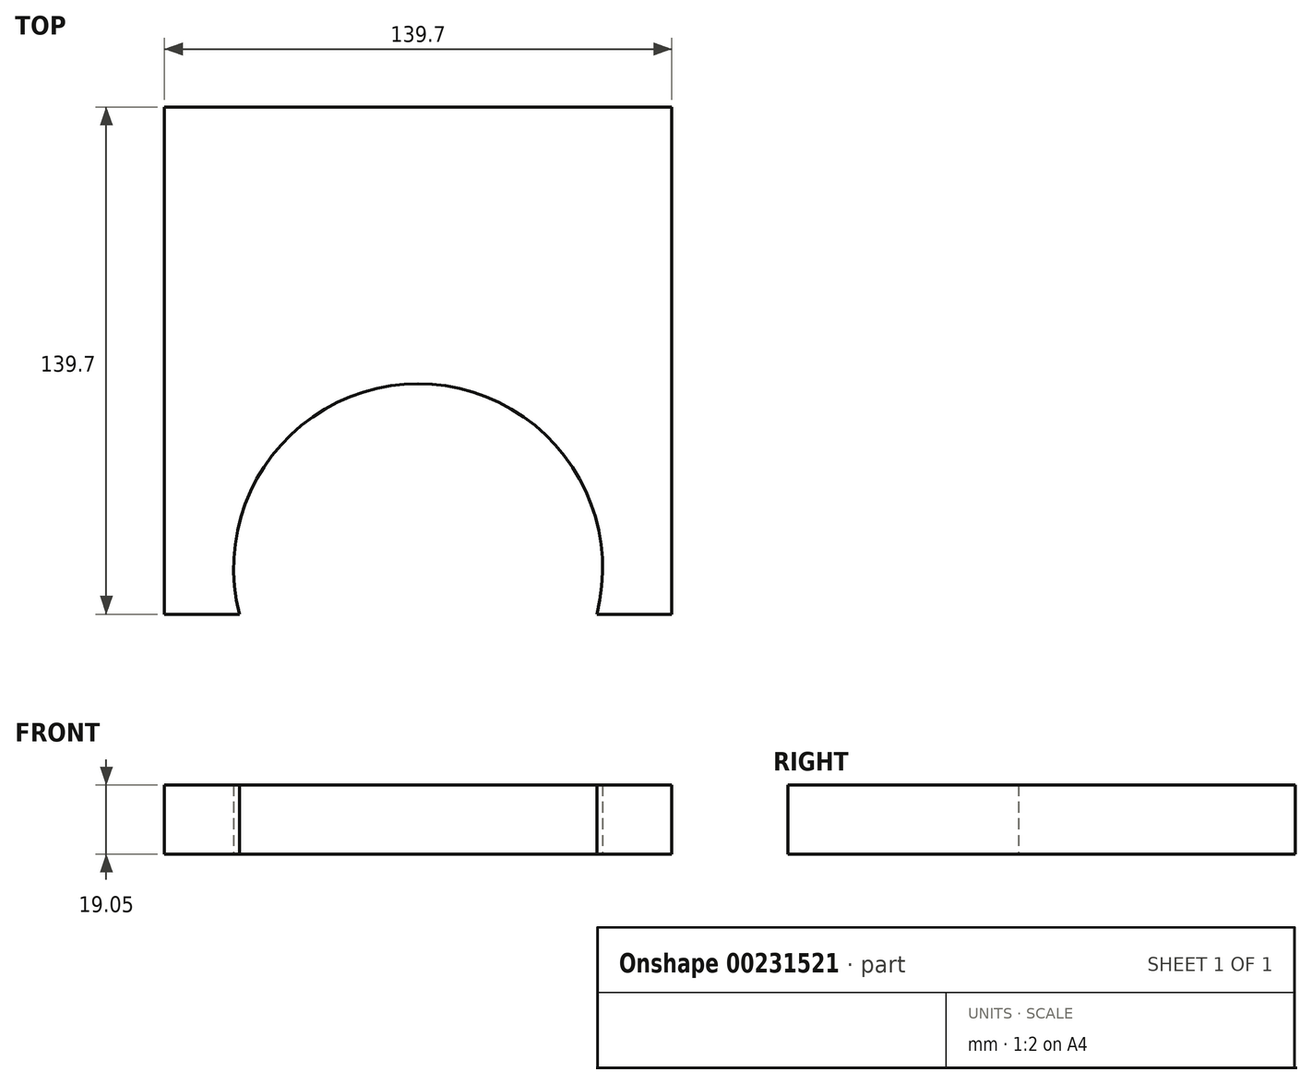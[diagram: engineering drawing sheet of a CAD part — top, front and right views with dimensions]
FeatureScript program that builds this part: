
annotation { "Feature Type Name" : "Feature", "Feature Type Description" : "" }
export const myFeature = defineFeature(function(context is Context, id is Id, definition is map)
    precondition{}
    {
        {
            var Q0;
            Q0=qCreatedBy(makeId("Top.planeOp"),FACE);
            var sketch = newSketch(context, id + "F0", { "sketchPlane" : qUnion([Q0])});
            skLineSegment(sketch, "E0.bottom", {"start": v(69.85, -69.85) * mm, "end": v(49.19, -69.85) * mm});
            skLineSegment(sketch, "E0.top", {"start": v(69.85, 69.85) * mm, "end": v(-69.85, 69.85) * mm});
            skLineSegment(sketch, "E0.left", {"start": v(69.85, -69.85) * mm, "end": v(69.85, 69.85) * mm});
            skLineSegment(sketch, "E0.right", {"start": v(-69.85, -69.85) * mm, "end": v(-69.85, 69.85) * mm});
            skPoint(sketch, "E0.middle", {"position": v(0, 0) * mm});
            skPoint(sketch, "E1.endSnap0", {"position": v(0, -69.85) * mm});
            skArc(sketch, "E2", {"start": v(49.19, -69.85) * mm, "mid": v(0, -6.35) * mm, "end": v(-49.19, -69.85) * mm});
            skLineSegment(sketch, "E3.trimOffspring", {"start": v(-49.19, -69.85) * mm, "end": v(-69.85, -69.85) * mm});
            skPoint(sketch, "E1.start.orphan", {"position": v(0, -69.85) * mm});
            skSolve(sketch);
        }
        {
            var Q0;
            Q0 = qSketchRegion(id + "F0", true);
            extrude(context, id + "F1", {"entities" : qUnion([Q0]), "depth" : 19.05 * mm});
        }
    });
